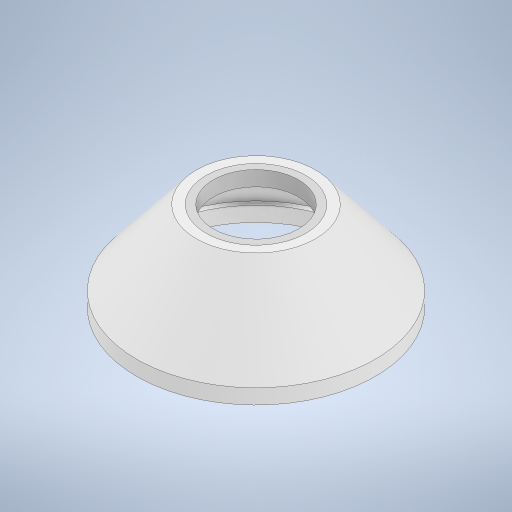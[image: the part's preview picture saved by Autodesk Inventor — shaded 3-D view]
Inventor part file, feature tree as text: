
AUTODESK INVENTOR PART (.ipt)
format: ipt  version: 2023 (Build 270158000, 158)  size: 605,184 bytes
history: native  units: mm
features: sketch x3, extrude x2, plane x1, loft x1, shell x1, other x1
ambient origin geometry x8: Origin, YZ Plane, XZ Plane, XY Plane, X Axis, Y Axis, Z Axis, Center Point
bodies: Solid1 (feature_tree)
feature tree (9):
  sketch  "Sketch1"  dims[d0=160.0mm d1=10.0mm]
  extrude  "Extrusion1"  Depth=10.0mm
  plane  "Work Plane1"
  loft  "Loft1"
  shell  "Shell1"  Thickness=25.0mm
  extrude  "Extrusion4"  TaperAngle=0.0deg  [1 undecoded]
  sketch  "Sketch2"  dims[d2=10.0mm d3=0.0mm d4=50.0mm d5=25.0mm]
  other  "Edges1"
  sketch  "Sketch4"  dims[d6=5.0mm d7=0.0mm d8=90.0deg d9=0.0mm d10=90.0deg d11=5.0mm d18=5.0mm d19=10.0mm d20=0.0mm]
note: 1 required parameter value undecoded (feature->parameter linkage not recoverable at this tier; creation-order binding heuristic only, values carry confidence <= 0.55)
